# Revit family: ledhighbay-lin-p_240w-dali-840-xas-em3_545001111000
name_source: partatom
category: Lighting Fixtures
units: mm (PartAtom-declared; Revit-internal decimal feet)

## family parameters
Cut with Voids When Loaded = No
Host = Face
Light Source = No
Part Type = Normal
Room Calculation Point = No
Round Connector Dimension = Use Diameter
Shared = No

## types (1)
- LEDHighbay-Lin-P 240W-DALI-840-XAS-EM3 (1 x LED, 43200 lm, 4000)
    Apparent Load = 240 VA
    Approval mark = CE, ENEC
    CIE Flux Codes = 69 90 98 100 100
    Color Rendering = 80
    Color Temperature = 4000
    Control Gear = Electronic ballast
    Default Elevation = 1800 mm
    Description = Highbay Performer Linear 240W-43200lm-4000K-25°x85°-DALI-Emergency 3h
    Frequency = 60 Hz
    Height = 60 mm  [stored 0.19685 ft]
    Lamp = 1 x LED
    Lamp Light Flux = 43200 lm
    Lamp count = 1
    Length = 680 mm
    Luminous efficacy = 180 lm/W
    Manufacturer = OPPLE
    ModVariant = No
    Model = 545001111000
    Mounting Place = Ceiling
    Mounting Type = Pendant
    Number of Poles = 1
    OnlyDefault = Yes
    Power Factor = 1
    Product Name = LEDHighbay-Lin-P 240W-DALI-840-XAS-EM3
    Product group = Pendant luminaire
    ProductGroupID = 9
    Protection Class = Protection class I
    Protection Degree = IP 66
    RLX_Detail_Level = 1
    RLX_Emergency_Light_Flux = 0 lm
    RLX_Emergency_Type = 0
    RLX_Emergency_Type_DB = No
    RlxData = <blob elided: 561729 chars, md5=bcf9e4d5>
    Socket = socket
    Standby Power = 0 W
    System Light Flux = 43200 lm
    System Power = 240 W
    Type Comments = Product without accessories
    Type Image = web_hb_linear_240w_300w.jpg
    URL = http://relux.com
    VarID = ---
    Voltage = 230 V
    Voltage Range = 220-240 V
    Weight = 0.00 kg
    Width = 325 mm

note: [stored X ft] marks values corroborated as IEEE doubles in the binary element streams (Revit-internal decimal feet)

## geometry (parser evidence)
native form markers: Blend x4, Sweep x14
no freeform markers — native parametric forms only
